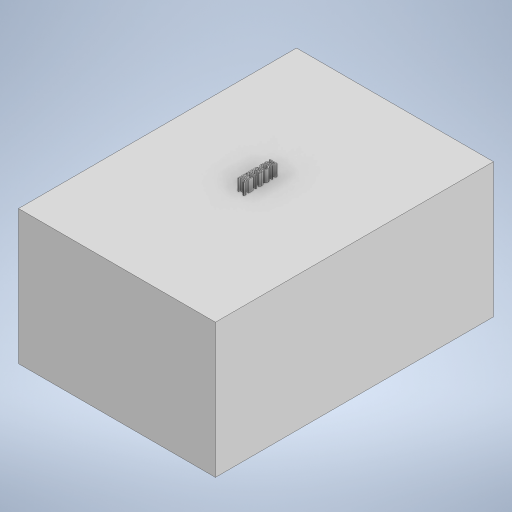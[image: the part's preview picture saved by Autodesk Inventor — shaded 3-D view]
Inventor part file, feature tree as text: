
AUTODESK INVENTOR PART (.ipt)
format: ipt  version: 2023 (Build 270158000, 158)  size: 281,088 bytes
history: native  units: mm
features: extrude x2, sketch x2, other x1
ambient origin geometry x8: Origin, YZ Plane, XZ Plane, XY Plane, X Axis, Y Axis, Z Axis, Center Point
bodies: Body1 (feature_tree)
feature tree (5):
  other  "Sólido1"
  extrude  "Extrusión1"  Depth=120.0mm
  extrude  "Extrusión2"  Depth=58.0mm TaperAngle=0.0deg
  sketch  "Boceto1"  dims[d0=85.0mm d1=120.0mm]
  sketch  "Boceto2"  dims[d2=58.0mm d3=0.0mm d4=5.0mm d5=0.0mm]
